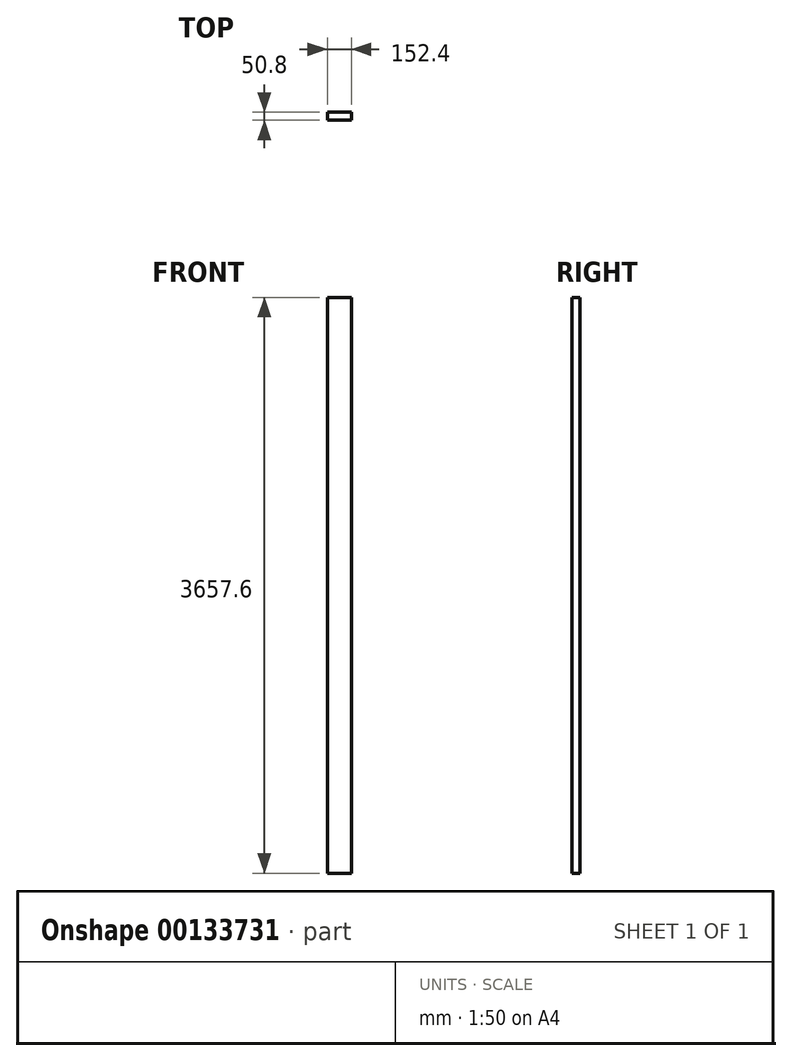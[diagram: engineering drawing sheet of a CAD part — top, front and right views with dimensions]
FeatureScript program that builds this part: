
annotation { "Feature Type Name" : "Feature", "Feature Type Description" : "" }
export const myFeature = defineFeature(function(context is Context, id is Id, definition is map)
    precondition{}
    {
        {
            var Q0;
            Q0=qCreatedBy(makeId("Top.planeOp"),FACE);
            var sketch = newSketch(context, id + "F0", { "sketchPlane" : qUnion([Q0])});
            skLineSegment(sketch, "E0.bottom", {"start": v(0, 0) * mm, "end": v(152.4, 0) * mm});
            skLineSegment(sketch, "E0.top", {"start": v(0, -50.8) * mm, "end": v(152.4, -50.8) * mm});
            skLineSegment(sketch, "E0.left", {"start": v(0, 0) * mm, "end": v(0, -50.8) * mm});
            skLineSegment(sketch, "E0.right", {"start": v(152.4, 0) * mm, "end": v(152.4, -50.8) * mm});
            skSolve(sketch);
        }
        {
            var Q0;
            Q0 = qSketchRegion(id + "F0", true);
            extrude(context, id + "F1", {"entities" : qUnion([Q0]), "depth" : 3657.6 * mm});
        }
    });
